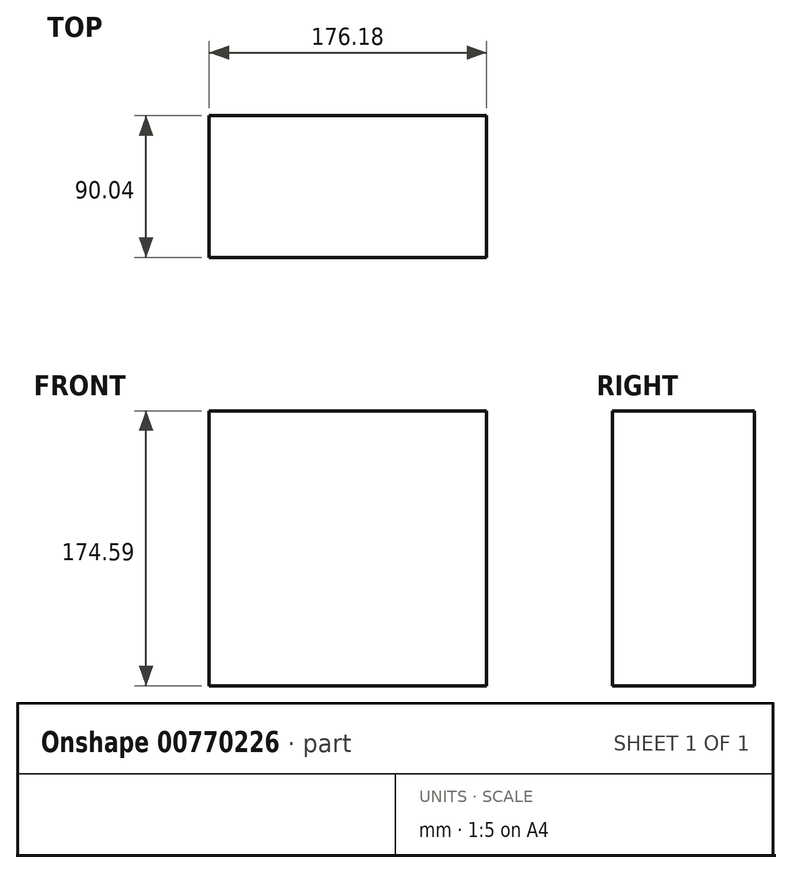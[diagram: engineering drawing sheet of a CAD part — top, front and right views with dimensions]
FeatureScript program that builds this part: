
annotation { "Feature Type Name" : "Feature", "Feature Type Description" : "" }
export const myFeature = defineFeature(function(context is Context, id is Id, definition is map)
    precondition{}
    {
        {
            var Q0;
            Q0=qCreatedBy(makeId("Right.planeOp"),FACE);
            var sketch = newSketch(context, id + "F0", { "sketchPlane" : qUnion([Q0])});
            skLineSegment(sketch, "E0.bottom", {"start": v(-43.42, 73.9) * mm, "end": v(46.62, 73.9) * mm});
            skLineSegment(sketch, "E0.top", {"start": v(-43.42, -100.69) * mm, "end": v(46.62, -100.69) * mm});
            skLineSegment(sketch, "E0.left", {"start": v(-43.42, 73.9) * mm, "end": v(-43.42, -100.69) * mm});
            skLineSegment(sketch, "E0.right", {"start": v(46.62, 73.9) * mm, "end": v(46.62, -100.69) * mm});
            skSolve(sketch);
        }
        {
            var Q0;
            Q0=makeQuery(id+"F0.imprint","IMPRINT",FACE,{"disambiguationData":[TD([[makeQuery(id+"F0.imprint","IMPRINT",EDGE,{"derivedFrom":sQuery(id+"F0.wireOp",EDGE,"E0.bottom")}),-1.0]])]});
            extrude(context, id + "F1", {"entities" : qUnion([Q0]), "depth" : 176.18 * mm, "offsetDistance" : 25.4 * mm});
        }
    });
